# Revit family: VFB_VFB Plus 256-450mm
name_source: partatom
category: Specialty Equipment
revit_build: Autodesk Revit 2015 (Build: 20160512_0715(x64)
units: mm (PartAtom-declared; Revit-internal decimal feet)

## types (194) — shared parameters
Depth = 75 mm  [stored 0.246063 ft]
Description = Firefly 102 Ventilated Fire Barrier
IFC Classification = Building Element Proxy
Length = 1000 mm
Manufacturer = Tenmat ltd
Material/Grade = Firefly 102
Performance = BS EN 1366-3:2009 & BS 476, ETA-12/0332, 1224-CPR-0341, CE Marked
URL = https://www.tenmat.com
Youtube Clip = https://www.youtube.com

## per-type parameters (varying)
| type | Seal Type | Tenmat Item Number | Width |
| VFB Plus 256.0 x 75.0 x 1000mm | VFB Plus 300 | I102MP25600075100000 | 256 mm  [stored 0.839895 ft] |
| VFB Plus 257.0 x 75.0 x 1000mm | VFB Plus 301 | I102MP25700075100000 | 257 mm  [stored 0.843176 ft] |
| VFB Plus 258.0 x 75.0 x 1000mm | VFB Plus 302 | I102MP25800075100000 | 258 mm  [stored 0.846457 ft] |
| VFB Plus 259.0 x 75.0 x 1000mm | VFB Plus 303 | I102MP25900075100000 | 259 mm  [stored 0.849738 ft] |
| VFB Plus 260.0 x 75.0 x 1000mm | VFB Plus 304 | I102MP26000075100000 | 260 mm  [stored 0.853018 ft] |
| VFB Plus 261.0 x 75.0 x 1000mm | VFB Plus 305 | I102MP26100075100000 | 261 mm |
| VFB Plus 262.0 x 75.0 x 1000mm | VFB Plus 306 | I102MP07500075100000
I102MP26200075100000 | 262 mm  [stored 0.85958 ft] |
| VFB Plus 263.0 x 75.0 x 1000mm | VFB Plus 307 | I102MP26300075100000 | 263 mm  [stored 0.862861 ft] |
| VFB Plus 264.0 x 75.0 x 1000mm | VFB Plus 308 | I102MP26400075100000 | 264 mm  [stored 0.866142 ft] |
| VFB Plus 265.0 x 75.0 x 1000mm | VFB Plus 309 | I102MP26500075100000 | 265 mm  [stored 0.869423 ft] |
| VFB Plus 266.0 x 75.0 x 1000mm | VFB Plus 310 | I102MP26600075100000 | 266 mm  [stored 0.872703 ft] |
| VFB Plus 267.0 x 75.0 x 1000mm | VFB Plus 311 | I102MP26700075100000
I102MP01600075100000 | 267 mm  [stored 0.875984 ft] |
| VFB Plus 268.0 x 75.0 x 1000mm | VFB Plus 312 | I102MP26800075100000 | 268 mm |
| VFB Plus 269.0 x 75.0 x 1000mm | VFB Plus 313 | I102MP26900075100000 | 269 mm  [stored 0.882546 ft] |
| VFB Plus 270.0 x 75.0 x 1000mm | VFB Plus 314 | I102MP27000075100000 | 270 mm  [stored 0.885827 ft] |
| VFB Plus 271.0 x 75.0 x 1000mm | VFB Plus 315 | I102MP27100075100000 | 271 mm  [stored 0.889108 ft] |
| VFB Plus 272.0 x 75.0 x 1000mm | VFB Plus 316 | I102MP27200075100000 | 272 mm |
| VFB Plus 273.0 x 75.0 x 1000mm | VFB Plus 317 | I102MP27300075100000 | 273 mm  [stored 0.895669 ft] |
| VFB Plus 274.0 x 75.0 x 1000mm | VFB Plus 318 | I102MP27400075100000 | 274 mm  [stored 0.89895 ft] |
| VFB Plus 275.0 x 75.0 x 1000mm | VFB Plus 319 | I102MP27500075100000 | 275 mm |
| VFB Plus 276.0 x 75.0 x 1000mm | VFB Plus 320 | I102MP27600075100000 | 276 mm  [stored 0.905512 ft] |
| VFB Plus 277.0 x 75.0 x 1000mm | VFB Plus 321 | I102MP27700075100000 | 277 mm  [stored 0.908793 ft] |
| VFB Plus 278.0 x 75.0 x 1000mm | VFB Plus 322 | I102MP27800075100000 | 278 mm  [stored 0.912073 ft] |
| VFB Plus 279.0 x 75.0 x 1000mm | VFB Plus 323 | I102MP27900075100000 | 279 mm |
| VFB Plus 280.0 x 75.0 x 1000mm | VFB Plus 324 | I102MP28000075100000 | 280 mm  [stored 0.918635 ft] |
| VFB Plus 281.0 x 75.0 x 1000mm | VFB Plus 325 | I102MP28100075100000 | 281 mm  [stored 0.921916 ft] |
| VFB Plus 282.0 x 75.0 x 1000mm | VFB Plus 326 | I102MP28200075100000 | 282 mm |
| VFB Plus 283.0 x 75.0 x 1000mm | VFB Plus 327 | I102MP28300075100000 | 283 mm  [stored 0.928478 ft] |
| VFB Plus 284.0 x 75.0 x 1000mm | VFB Plus 328 | I102MP28400075100000 | 284 mm  [stored 0.931759 ft] |
| VFB Plus 285.0 x 75.0 x 1000mm | VFB Plus 329 | I102MP28500075100000 | 285 mm  [stored 0.935039 ft] |
| VFB Plus 286.0 x 75.0 x 1000mm | VFB Plus 330 | I102MP28600075100000 | 286 mm |
| VFB Plus 287.0 x 75.0 x 1000mm | VFB Plus 331 | I102MP28700075100000 | 287 mm  [stored 0.941601 ft] |
| VFB Plus 288.0 x 75.0 x 1000mm | VFB Plus 332 | I102MP28800075100000 | 288 mm  [stored 0.944882 ft] |
| VFB Plus 289.0 x 75.0 x 1000mm | VFB Plus 333 | I102MP28900075100000 | 289 mm  [stored 0.948163 ft] |
| VFB Plus 290.0 x 75.0 x 1000mm | VFB Plus 334 | I102MP29000075100000 | 290 mm  [stored 0.951444 ft] |
| VFB Plus 291.0 x 75.0 x 1000mm | VFB Plus 335 | I102MP29100075100000 | 291 mm  [stored 0.954724 ft] |
| VFB Plus 292.0 x 75.0 x 1000mm | VFB Plus 336 | I102MP29200075100000 | 292 mm  [stored 0.958005 ft] |
| VFB Plus 293.0 x 75.0 x 1000mm | VFB Plus 337 | I102MP29300075100000 | 293 mm |
| VFB Plus 294.0 x 75.0 x 1000mm | VFB Plus 338 | I102MP29400075100000 | 294 mm  [stored 0.964567 ft] |
| VFB Plus 295.0 x 75.0 x 1000mm | VFB Plus 339 | I102MP29500075100000 | 295 mm |
| VFB Plus 296.0 x 75.0 x 1000mm | VFB Plus 340 | I102MP29600075100000 | 296 mm |
| VFB Plus 297.0 x 75.0 x 1000mm | VFB Plus 341 | I102MP29700075100000 | 297 mm |
| VFB Plus 298.0 x 75.0 x 1000mm | VFB Plus 342 | I102MP29800075100000 | 298 mm |
| VFB Plus 299.0 x 75.0 x 1000mm | VFB Plus 343 | I102MP29900075100000 | 299 mm |
| VFB Plus 300.0 x 75.0 x 1000mm | VFB Plus 344 | I102MP30000075100000 | 300 mm |
| VFB Plus 301.0 x 75.0 x 1000mm | VFB Plus 345 | I102MP30100075100000 | 301 mm |
| VFB Plus 302.0 x 75.0 x 1000mm | VFB Plus 346 | I102MP30200075100000 | 302 mm |
| VFB Plus 303.0 x 75.0 x 1000mm | VFB Plus 347 | I102MP30300075100000 | 303 mm |
| VFB Plus 304.0 x 75.0 x 1000mm | VFB Plus 348 | I102MP30400075100000 | 304 mm |
| VFB Plus 305.0 x 75.0 x 1000mm | VFB Plus 349 | I102MP30500075100000 | 305 mm |
| VFB Plus 306.0 x 75.0 x 1000mm | VFB Plus 350 | I102MP30600075100000 | 306 mm |
| VFB Plus 307.0 x 75.0 x 1000mm | VFB Plus 351 | I102MP30700075100000 | 307 mm |
| VFB Plus 308.0 x 75.0 x 1000mm | VFB Plus 352 | I102MP30800075100000 | 308 mm |
| VFB Plus 309.0 x 75.0 x 1000mm | VFB Plus 353 | I102MP30900075100000
I102MP01600075100000 | 309 mm |
| VFB Plus 310.0 x 75.0 x 1000mm | VFB Plus 354 | I102MP31000075100000 | 310 mm |
| VFB Plus 311.0 x 75.0 x 1000mm | VFB Plus 355 | I102MP31100075100000 | 311 mm |
| VFB Plus 312.0 x 75.0 x 1000mm | VFB Plus 356 | I102MP31200075100000 | 312 mm |
| VFB Plus 313.0 x 75.0 x 1000mm | VFB Plus 357 | I102MP31300075100000 | 313 mm |
| VFB Plus 314.0 x 75.0 x 1000mm | VFB Plus 358 | I102MP31400075100000 | 314 mm |
| VFB Plus 315.0 x 75.0 x 1000mm | VFB Plus 359 | I102MP31500075100000 | 315 mm |
| VFB Plus 316.0 x 75.0 x 1000mm | VFB Plus 360 | I102MP31600075100000 | 316 mm |
| VFB Plus 317.0 x 75.0 x 1000mm | VFB Plus 361 | I102MP31700075100000 | 317 mm |
| VFB Plus 318.0 x 75.0 x 1000mm | VFB Plus 362 | I102MP31800075100000 | 318 mm |
| VFB Plus 319.0 x 75.0 x 1000mm | VFB Plus 363 | I102MP31900075100000 | 319 mm |
| VFB Plus 320.0 x 75.0 x 1000mm | VFB Plus 364 | I102MP32000075100000 | 320 mm |
| VFB Plus 321.0 x 75.0 x 1000mm | VFB Plus 365 | I102MP32100075100000 | 321 mm |
| VFB Plus 322.0 x 75.0 x 1000mm | VFB Plus 366 | I102MP32200075100000 | 322 mm |
| VFB Plus 323.0 x 75.0 x 1000mm | VFB Plus 367 | I102MP32300075100000 | 323 mm |
| VFB Plus 324.0 x 75.0 x 1000mm | VFB Plus 368 | I102MP32400075100000 | 324 mm |
| VFB Plus 325.0 x 75.0 x 1000mm | VFB Plus 369 | I102MP32500075100000 | 325 mm |
| VFB Plus 326.0 x 75.0 x 1000mm | VFB Plus 370 | I102MP32600075100000 | 326 mm |
| VFB Plus 327.0 x 75.0 x 1000mm | VFB Plus 371 | I102MP32700075100000 | 327 mm |
| VFB Plus 328.0 x 75.0 x 1000mm | VFB Plus 372 | I102MP32800075100000 | 328 mm |
| VFB Plus 329.0 x 75.0 x 1000mm | VFB Plus 373 | I102MP32900075100000 | 329 mm |
| VFB Plus 330.0 x 75.0 x 1000mm | VFB Plus 374 | I102MP33000075100000 | 330 mm |
| VFB Plus 331.0 x 75.0 x 1000mm | VFB Plus 375 | I102MP33100075100000 | 331 mm |
| VFB Plus 332.0 x 75.0 x 1000mm | VFB Plus 376 | I102MP33200075100000
I102MP01600075100000 | 332 mm |
| VFB Plus 333.0 x 75.0 x 1000mm | VFB Plus 377 | I102MP33300075100000 | 333 mm |
| VFB Plus 334.0 x 75.0 x 1000mm | VFB Plus 378 | I102MP33400075100000 | 334 mm |
| VFB Plus 335.0 x 75.0 x 1000mm | VFB Plus 379 | I102MP33500075100000 | 335 mm |
| VFB Plus 336.0 x 75.0 x 1000mm | VFB Plus 380 | I102MP33600075100000 | 336 mm |
| VFB Plus 337.0 x 75.0 x 1000mm | VFB Plus 381 | I102MP33700075100000 | 337 mm |
| VFB Plus 338.0 x 75.0 x 1000mm | VFB Plus 382 | I102MP33800075100000 | 338 mm |
| VFB Plus 339.0 x 75.0 x 1000mm | VFB Plus 383 | I102MP33900075100000 | 339 mm |
| VFB Plus 340.0 x 75.0 x 1000mm | VFB Plus 384 | I102MP34000075100000 | 340 mm |
| VFB Plus 341.0 x 75.0 x 1000mm | VFB Plus 385 | I102MP34100075100000 | 341 mm |
| VFB Plus 342.0 x 75.0 x 1000mm | VFB Plus 386 | I102MP34200075100000 | 342 mm |
| VFB Plus 343.0 x 75.0 x 1000mm | VFB Plus 387 | I102MP34300075100000 | 343 mm |
| VFB Plus 344.0 x 75.0 x 1000mm | VFB Plus 388 | I102MP34400075100000 | 344 mm |
| VFB Plus 345.0 x 75.0 x 1000mm | VFB Plus 389 | I102MP34500075100000 | 345 mm |
| VFB Plus 346.0 x 75.0 x 1000mm | VFB Plus 390 | I102MP34600075100000 | 346 mm |
| VFB Plus 347.0 x 75.0 x 1000mm | VFB Plus 391 | I102MP34700075100000 | 347 mm |
| VFB Plus 348.0 x 75.0 x 1000mm | VFB Plus 392 | I102MP34800075100000 | 348 mm |
| VFB Plus 349.0 x 75.0 x 1000mm | VFB Plus 393 | I102MP34900075100000 | 349 mm |
| VFB Plus 350.0 x 75.0 x 1000mm | VFB Plus 394 | I102MP35000075100000 | 350 mm |
| VFB Plus 351.0 x 75.0 x 1000mm | VFB Plus 395 | I102MP35100075100000 | 351 mm |
| VFB Plus 352.0 x 75.0 x 1000mm | VFB Plus 396 | I102MP35200075100000 | 352 mm |
| VFB Plus 353.0 x 75.0 x 1000mm | VFB Plus 397 | I102MP35300075100000 | 353 mm |
| VFB Plus 354.0 x 75.0 x 1000mm | VFB Plus 398 | I102MP35400075100000 | 354 mm |
| VFB Plus 355.0 x 75.0 x 1000mm | VFB Plus 399 | I102MP35500075100000 | 355 mm |
| VFB Plus 356.0 x 75.0 x 1000mm | VFB Plus 400 | I102MP35600075100000 | 356 mm |
| VFB Plus 357.0 x 75.0 x 1000mm | VFB Plus 401 | I102MP35700075100000 | 357 mm |
| VFB Plus 358.0 x 75.0 x 1000mm | VFB Plus 402 | I102MP35800075100000 | 358 mm |
| VFB Plus 359.0 x 75.0 x 1000mm | VFB Plus 403 | I102MP35900075100000 | 359 mm |
| VFB Plus 360.0 x 75.0 x 1000mm | VFB Plus 404 | I102MP36000075100000 | 360 mm |
| VFB Plus 361.0 x 75.0 x 1000mm | VFB Plus 405 | I102MP36100075100000 | 361 mm |
| VFB Plus 362.0 x 75.0 x 1000mm | VFB Plus 406 | I102MP36200075100000 | 362 mm |
| VFB Plus 363.0 x 75.0 x 1000mm | VFB Plus 407 | I102MP36300075100000 | 363 mm |
| VFB Plus 364.0 x 75.0 x 1000mm | VFB Plus 408 | I102MP36400075100000 | 364 mm |
| VFB Plus 365.0 x 75.0 x 1000mm | VFB Plus 409 | I102MP36500075100000 | 365 mm |
| VFB Plus 366.0 x 75.0 x 1000mm | VFB Plus 410 | I102MP36600075100000 | 366 mm |
| VFB Plus 367.0 x 75.0 x 1000mm | VFB Plus 411 | I102MP36700075100000 | 367 mm |
| VFB Plus 368.0 x 75.0 x 1000mm | VFB Plus 412 | I102MP36800075100000 | 368 mm |
| VFB Plus 369.0 x 75.0 x 1000mm | VFB Plus 413 | I102MP36900075100000 | 369 mm |
| VFB Plus 370.0 x 75.0 x 1000mm | VFB Plus 414 | I102MP37000075100000 | 370 mm |
| VFB Plus 371.0 x 75.0 x 1000mm | VFB Plus 415 | I102MP37100075100000 | 371 mm |
| VFB Plus 372.0 x 75.0 x 1000mm | VFB Plus 416 | I102MP37200075100000 | 372 mm |
| VFB Plus 374.0 x 75.0 x 1000mm | VFB Plus 417 | I102MP37400075100000 | 374 mm |
| VFB Plus 375.0 x 75.0 x 1000mm | VFB Plus 418 | I102MP37500075100000 | 375 mm |
| VFB Plus 376.0 x 75.0 x 1000mm | VFB Plus 419 | I102MP37600075100000 | 376 mm |
| VFB Plus 377.0 x 75.0 x 1000mm | VFB Plus 420 | I102MP37700075100000 | 377 mm |
| VFB Plus 378.0 x 75.0 x 1000mm | VFB Plus 421 | I102MP37800075100000 | 378 mm |
| VFB Plus 379.0 x 75.0 x 1000mm | VFB Plus 422 | I102MP37900075100000 | 379 mm |
| VFB Plus 380.0 x 75.0 x 1000mm | VFB Plus 422 | I102MP38000075100000 | 380 mm |
| VFB Plus 381.0 x 75.0 x 1000mm | VFB Plus 423 | I102MP38100075100000 | 381 mm |
| VFB Plus 382.0 x 75.0 x 1000mm | VFB Plus 424 | I102MP38200075100000 | 382 mm |
| VFB Plus 383.0 x 75.0 x 1000mm | VFB Plus 425 | I102MP38300075100000 | 383 mm |
| VFB Plus 384.0 x 75.0 x 1000mm | VFB Plus 426 | I102MP38400075100000 | 384 mm |
| VFB Plus 385.0 x 75.0 x 1000mm | VFB Plus 427 | I102MP38500075100000 | 385 mm |
| VFB Plus 386.0 x 75.0 x 1000mm | VFB Plus 428 | I102MP38600075100000 | 386 mm |
| VFB Plus 387.0 x 75.0 x 1000mm | VFB Plus 429 | I102MP38700075100000 | 387 mm |
| VFB Plus 388.0 x 75.0 x 1000mm | VFB Plus 430 | I102MP38800075100000
I102MP01600075100000 | 388 mm |
| VFB Plus 389.0 x 75.0 x 1000mm | VFB Plus 431 | I102MP38900075100000 | 389 mm |
| VFB Plus 390.0 x 75.0 x 1000mm | VFB Plus 432 | I102MP39000075100000 | 390 mm |
| VFB Plus 391.0 x 75.0 x 1000mm | VFB Plus 433 | I102MP39100075100000 | 391 mm |
| VFB Plus 392.0 x 75.0 x 1000mm | VFB Plus 434 | I102MP39200075100000 | 392 mm |
| VFB Plus 393.0 x 75.0 x 1000mm | VFB Plus 435 | I102MP39300075100000 | 393 mm |
| VFB Plus 394.0 x 75.0 x 1000mm | VFB Plus 435 | I102MP39400075100000 | 394 mm |
| VFB Plus 395.0 x 75.0 x 1000mm | VFB Plus 436 | I102MP39500075100000 | 395 mm |
| VFB Plus 396.0 x 75.0 x 1000mm | VFB Plus 437 | I102MP39600075100000 | 396 mm |
| VFB Plus 397.0 x 75.0 x 1000mm | VFB Plus 438 | I102MP39700075100000 | 397 mm |
| VFB Plus 398.0 x 75.0 x 1000mm | VFB Plus 439 | I102MP39800075100000 | 398 mm |
| VFB Plus 399.0 x 75.0 x 1000mm | VFB Plus 440 | I102MP39900075100000 | 399 mm |
| VFB Plus 400.0 x 75.0 x 1000mm | VFB Plus 441 | I102MP40000075100000 | 400 mm |
| VFB Plus 401.0 x 75.0 x 1000mm | VFB Plus 442 | I102MP40100075100000 | 401 mm |
| VFB Plus 402.0 x 75.0 x 1000mm | VFB Plus 443 | I102MP40200075100000 | 402 mm |
| VFB Plus 403.0 x 75.0 x 1000mm | VFB Plus 444 | I102MP40300075100000 | 403 mm |
| VFB Plus 404.0 x 75.0 x 1000mm | VFB Plus 445 | I102MP40500075100000 | 405 mm |
| VFB Plus 405.0 x 75.0 x 1000mm | VFB Plus 446 | I102MP40500075100000 | 405 mm |
| VFB Plus 406.0 x 75.0 x 1000mm | VFB Plus 447 | I102MP40600075100000 | 406 mm |
| VFB Plus 407.0 x 75.0 x 1000mm | VFB Plus 448 | I102MP40700075100000 | 407 mm |
| VFB Plus 408.0 x 75.0 x 1000mm | VFB Plus 449 | I102MP40800075100000 | 408 mm |
| VFB Plus 409.0 x 75.0 x 1000mm | VFB Plus 450 | I102MP40900075100000 | 409 mm |
| VFB Plus 410.0 x 75.0 x 1000mm | VFB Plus 451 | I102MP41000075100000 | 410 mm |
| VFB Plus 411.0 x 75.0 x 1000mm | VFB Plus 452 | I102MP41100075100000 | 411 mm |
| VFB Plus 412.0 x 75.0 x 1000mm | VFB Plus 453 | I102MP41200075100000 | 412 mm |
| VFB Plus 413.0 x 75.0 x 1000mm | VFB Plus 454 | I102MP41300075100000 | 413 mm |
| VFB Plus 414.0 x 75.0 x 1000mm | VFB Plus 455 | I102MP41400075100000 | 414 mm |
| VFB Plus 415.0 x 75.0 x 1000mm | VFB Plus 456 | I102MP41500075100000 | 415 mm |
| VFB Plus 416.0 x 75.0 x 1000mm | VFB Plus 457 | I102MP41600075100000 | 416 mm |
| VFB Plus 417.0 x 75.0 x 1000mm | VFB Plus 458 | I102MP41700075100000 | 417 mm |
| VFB Plus 418.0 x 75.0 x 1000mm | VFB Plus 459 | I102MP41800075100000 | 418 mm |
| VFB Plus 419.0 x 75.0 x 1000mm | VFB Plus 460 | I102MP41900075100000 | 419 mm |
| VFB Plus 420.0 x 75.0 x 1000mm | VFB Plus 461 | I102MP42000075100000 | 420 mm |
| VFB Plus 421.0 x 75.0 x 1000mm | VFB Plus 462 | I102MP42100075100000 | 421 mm |
| VFB Plus 422.0 x 75.0 x 1000mm | VFB Plus 463 | I102MP42200075100000 | 422 mm |
| VFB Plus 423.0 x 75.0 x 1000mm | VFB Plus 464 | I102MP42300075100000 | 423 mm |
| VFB Plus 424.0 x 75.0 x 1000mm | VFB Plus 465 | I102MP42400075100000 | 424 mm |
| VFB Plus 425.0 x 75.0 x 1000mm | VFB Plus 466 | I102MP42500075100000 | 425 mm |
| VFB Plus 426.0 x 75.0 x 1000mm | VFB Plus 467 | I102MP42600075100000 | 426 mm |
| VFB Plus 427.0 x 75.0 x 1000mm | VFB Plus 468 | I102MP42700075100000 | 427 mm |
| VFB Plus 428.0 x 75.0 x 1000mm | VFB Plus 469 | I102MP42800075100000 | 428 mm |
| VFB Plus 429.0 x 75.0 x 1000mm | VFB Plus 470 | I102MP42900075100000 | 429 mm |
| VFB Plus 430.0 x 75.0 x 1000mm | VFB Plus 471 | I102MP43000075100000 | 430 mm |
| VFB Plus 431.0 x 75.0 x 1000mm | VFB Plus 472 | I102MP43100075100000 | 431 mm |
| VFB Plus 432.0 x 75.0 x 1000mm | VFB Plus 473 | I102MP43200075100000 | 432 mm |
| VFB Plus 433.0 x 75.0 x 1000mm | VFB Plus 474 | I102MP43300075100000 | 433 mm |
| VFB Plus 434.0 x 75.0 x 1000mm | VFB Plus 475 | I102MP43400075100000 | 434 mm |
| VFB Plus 435.0 x 75.0 x 1000mm | VFB Plus 476 | I102MP43500075100000 | 435 mm |
| VFB Plus 436.0 x 75.0 x 1000mm | VFB Plus 477 | I102MP43600075100000 | 436 mm |
| VFB Plus 437.0 x 75.0 x 1000mm | VFB Plus 478 | I102MP43700075100000 | 437 mm |
| VFB Plus 438.0 x 75.0 x 1000mm | VFB Plus 479 | I102MP43800075100000 | 438 mm |
| VFB Plus 439.0 x 75.0 x 1000mm | VFB Plus 480 | I102MP43900075100000 | 439 mm |
| VFB Plus 440.0 x 75.0 x 1000mm | VFB Plus 481 | I102MP44000075100000 | 440 mm |
| VFB Plus 441.0 x 75.0 x 1000mm | VFB Plus 482 | I102MP44100075100000 | 441 mm |
| VFB Plus 442.0 x 75.0 x 1000mm | VFB Plus 483 | I102MP44200075100000 | 442 mm |
| VFB Plus 443.0 x 75.0 x 1000mm | VFB Plus 484 | I102MP44300075100000
I102MP01600075100000 | 443 mm |
| VFB Plus 444.0 x 75.0 x 1000mm | VFB Plus 485 | I102MP44400075100000 | 444 mm |
| VFB Plus 445.0 x 75.0 x 1000mm | VFB Plus 486 | I102MP44500075100000 | 445 mm |
| VFB Plus 446.0 x 75.0 x 1000mm | VFB Plus 487 | I102MP44600075100000 | 446 mm |
| VFB Plus 447.0 x 75.0 x 1000mm | VFB Plus 488 | I102MP44700075100000
I102MP01600075100000 | 447 mm |
| VFB Plus 448.0 x 75.0 x 1000mm | VFB Plus 489 | I102MP44800075100000 | 448 mm |
| VFB Plus 449.0 x 75.0 x 1000mm | VFB Plus 490 | I102MP44900075100000 | 449 mm |
| VFB Plus 450.0 x 75.0 x 1000mm | VFB Plus 491 | I102MP45000075100000 | 450 mm |

note: [stored X ft] marks values corroborated as IEEE doubles in the binary element streams (Revit-internal decimal feet)

## geometry (parser evidence)
native form markers: Blend x2, Sweep x11
no freeform markers — native parametric forms only
